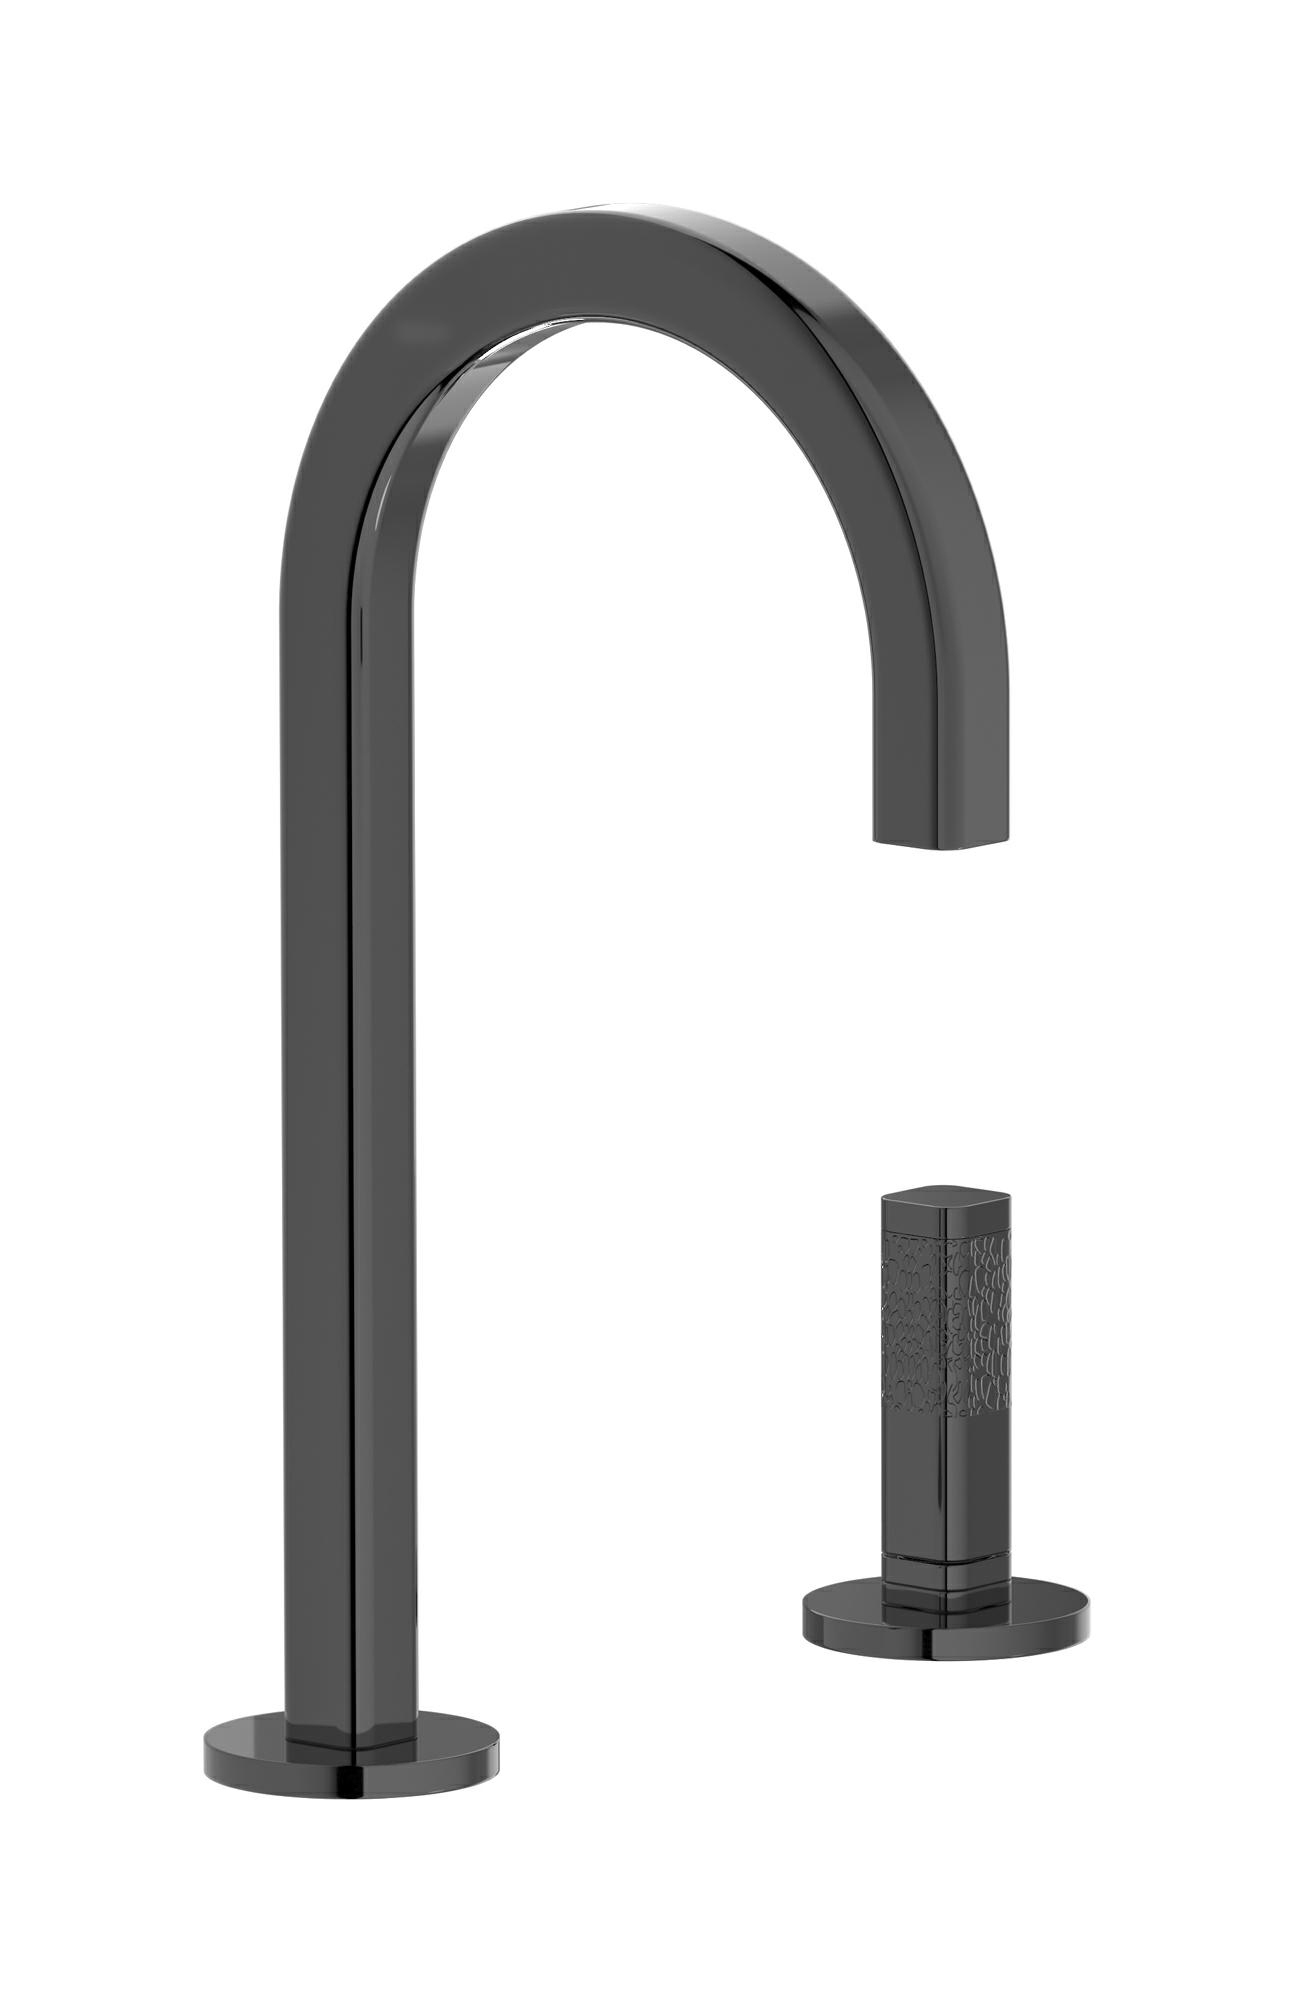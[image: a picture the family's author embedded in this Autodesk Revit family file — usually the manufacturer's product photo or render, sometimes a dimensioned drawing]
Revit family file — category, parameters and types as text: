
# Revit family: EI394_4
name_source: partatom
category: Apparecchi idraulici
units: mm (PartAtom-declared; Revit-internal decimal feet)

## family parameters
Basato su piano di lavoro = No
Condiviso = No
Mantieni orientamento annotazione = No
Numero OmniClass = 23.45.55.17
Punto di calcolo locali = No
Quota connettore circolare = Usa diametro
Sempre verticale = Sì
Taglio con vuoti quando caricato = No
Tipo di parte = Normale
Titolo OmniClass = Mixing Faucets

## types (12) — shared parameters
Cold water flow = 0,0 L/s
Cold water inlet = 10 mm  [stored 0.0328084 ft]
Commenti sul tipo = Washbasin
Connessione CW = No
Connessione HW = No
Connessione di scarico = No
Connessione di ventilazione = No
Descrizione = Washbasin two hole mixer
Hot water inlet = 10 mm  [stored 0.0328084 ft]
Produttore = IB Rubinetterie S.p.A.
URL = https://www.weareib.it
zero-valued in all types: Prospetto di default

## per-type parameters (varying)
| type | Finishes surface | Immagine tipo | Modello |
| Chrome | IB_Chrome | EI394CC_4.jpg | EI394CC_4 |
| Brushed nickel | IB_Brushed nickel | EI394SS_4.jpg | EI394SS_4 |
| Matt black | IB_matt black | EI394NP_4.jpg | EI394NP_4 |
| Natural brass | IB_Brass | EI394ON_4.jpg | EI394ON_4 |
| Black chrome | IB_Black chrome | EI394CF_4.jpg | EI394CF_4 |
| Brushed black chrome | IB_Brushed black chrome | EI394CS_4.jpg | EI394CS_4 |
| Pale gold | IB_Pale gold | EI394IS_4.jpg | EI394IS_4 |
| Brushed pale gold | IB_brushed pale gold | <Nessuno> | EI394IS_3 |
| Rose gold | IB_Rose gold | EI394RS_4.jpg | EI394RS_4 |
| Brushed rose gold | IB_Brushed rose gold | EI394SR_4.jpg | EI394SR_4 |
| Gold | IB_gold | EI394OO_4.jpg | EI394OO_4 |
| Brushed gold | IB_gold | EI394OS_4.jpg | EI394OS_4 |

note: [stored X ft] marks values corroborated as IEEE doubles in the binary element streams (Revit-internal decimal feet)
